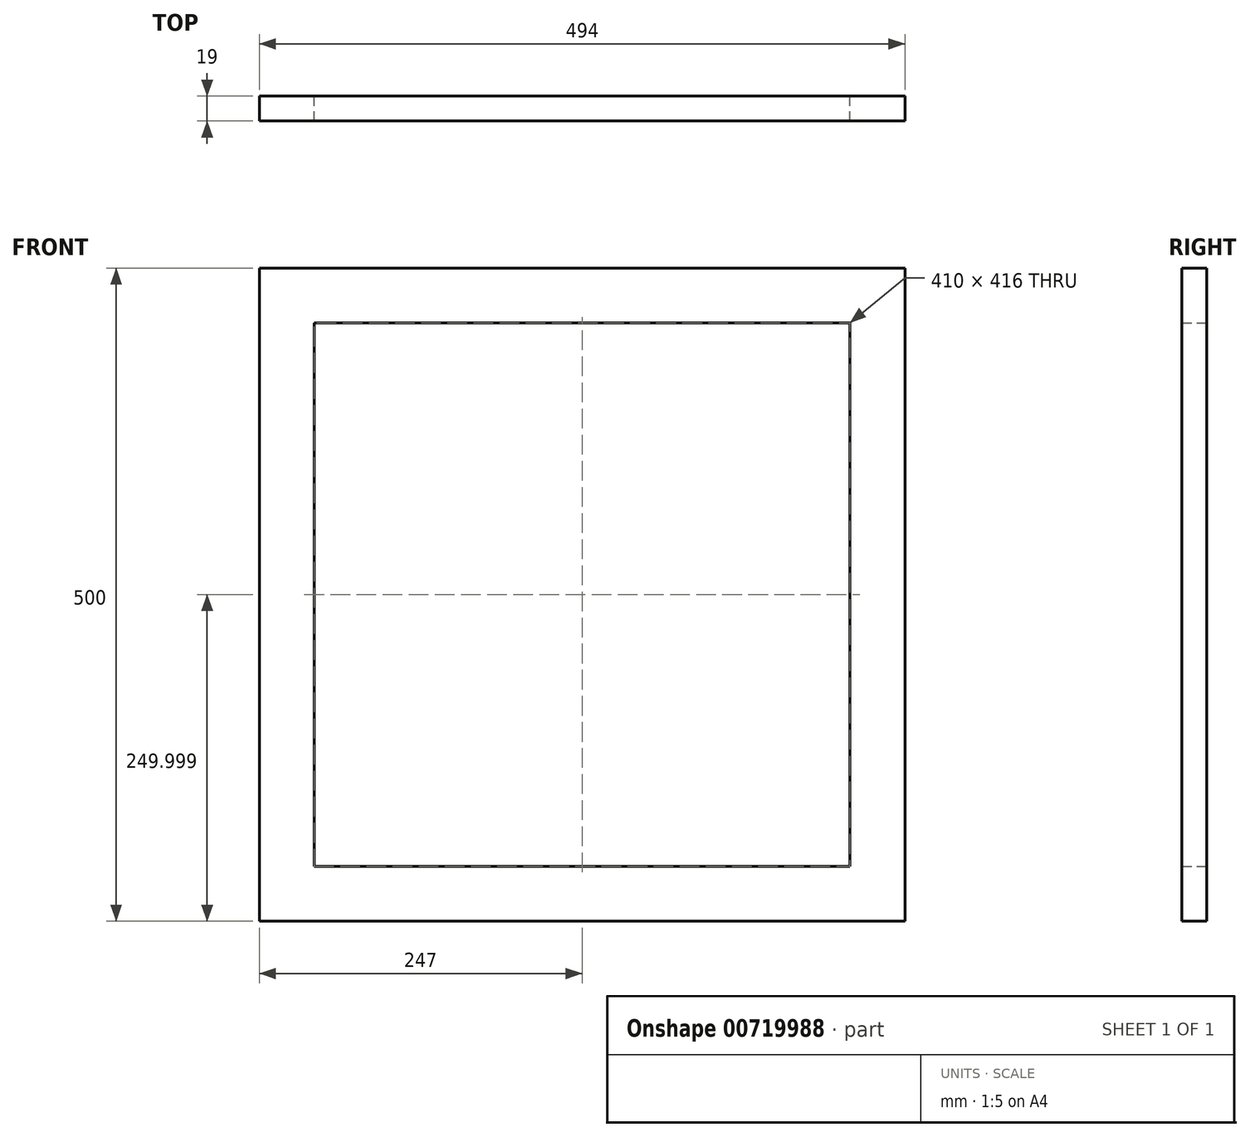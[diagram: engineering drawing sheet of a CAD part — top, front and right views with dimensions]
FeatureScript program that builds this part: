
annotation { "Feature Type Name" : "Feature", "Feature Type Description" : "" }
export const myFeature = defineFeature(function(context is Context, id is Id, definition is map)
    precondition{}
    {
        {
            var Q0;
            Q0=qCreatedBy(makeId("Front.planeOp"),FACE);
            var sketch = newSketch(context, id + "F0", { "sketchPlane" : qUnion([Q0])});
            skLineSegment(sketch, "E0.bottom", {"start": v(205, 194.53) * mm, "end": v(-205, 194.53) * mm});
            skLineSegment(sketch, "E0.top", {"start": v(205, 236.53) * mm, "end": v(-205, 236.53) * mm});
            skLineSegment(sketch, "E0.left", {"start": v(205, 194.53) * mm, "end": v(205, 236.53) * mm});
            skLineSegment(sketch, "E0.right", {"start": v(-205, 194.53) * mm, "end": v(-205, 236.53) * mm});
            skPoint(sketch, "E0.middle", {"position": v(0, 215.53) * mm});
            skLineSegment(sketch, "E1.bottom", {"start": v(-205, 236.53) * mm, "end": v(-247, 236.53) * mm});
            skLineSegment(sketch, "E1.top", {"start": v(-205, -263.47) * mm, "end": v(-247, -263.47) * mm});
            skLineSegment(sketch, "E1.left", {"start": v(-205, 236.53) * mm, "end": v(-205, -263.47) * mm});
            skLineSegment(sketch, "E1.right", {"start": v(-247, 236.53) * mm, "end": v(-247, -263.47) * mm});
            skLineSegment(sketch, "E2.bottom", {"start": v(-205, -263.47) * mm, "end": v(205, -263.47) * mm});
            skLineSegment(sketch, "E2.top", {"start": v(-205, -221.47) * mm, "end": v(205, -221.47) * mm});
            skLineSegment(sketch, "E2.left", {"start": v(-205, -263.47) * mm, "end": v(-205, -221.47) * mm});
            skLineSegment(sketch, "E2.right", {"start": v(205, -263.47) * mm, "end": v(205, -221.47) * mm});
            skLineSegment(sketch, "E3.bottom", {"start": v(205, -263.47) * mm, "end": v(247, -263.47) * mm});
            skLineSegment(sketch, "E3.top", {"start": v(205, 236.53) * mm, "end": v(247, 236.53) * mm});
            skLineSegment(sketch, "E3.left", {"start": v(205, -263.47) * mm, "end": v(205, 236.53) * mm});
            skLineSegment(sketch, "E3.right", {"start": v(247, -263.47) * mm, "end": v(247, 236.53) * mm});
            skSolve(sketch);
        }
        {
            var Q0;
            Q0 = qSketchRegion(id + "F0", true);
            extrude(context, id + "F1", {"entities" : qUnion([Q0]), "depth" : 19 * mm, "offsetDistance" : 25 * mm});
        }
    });
